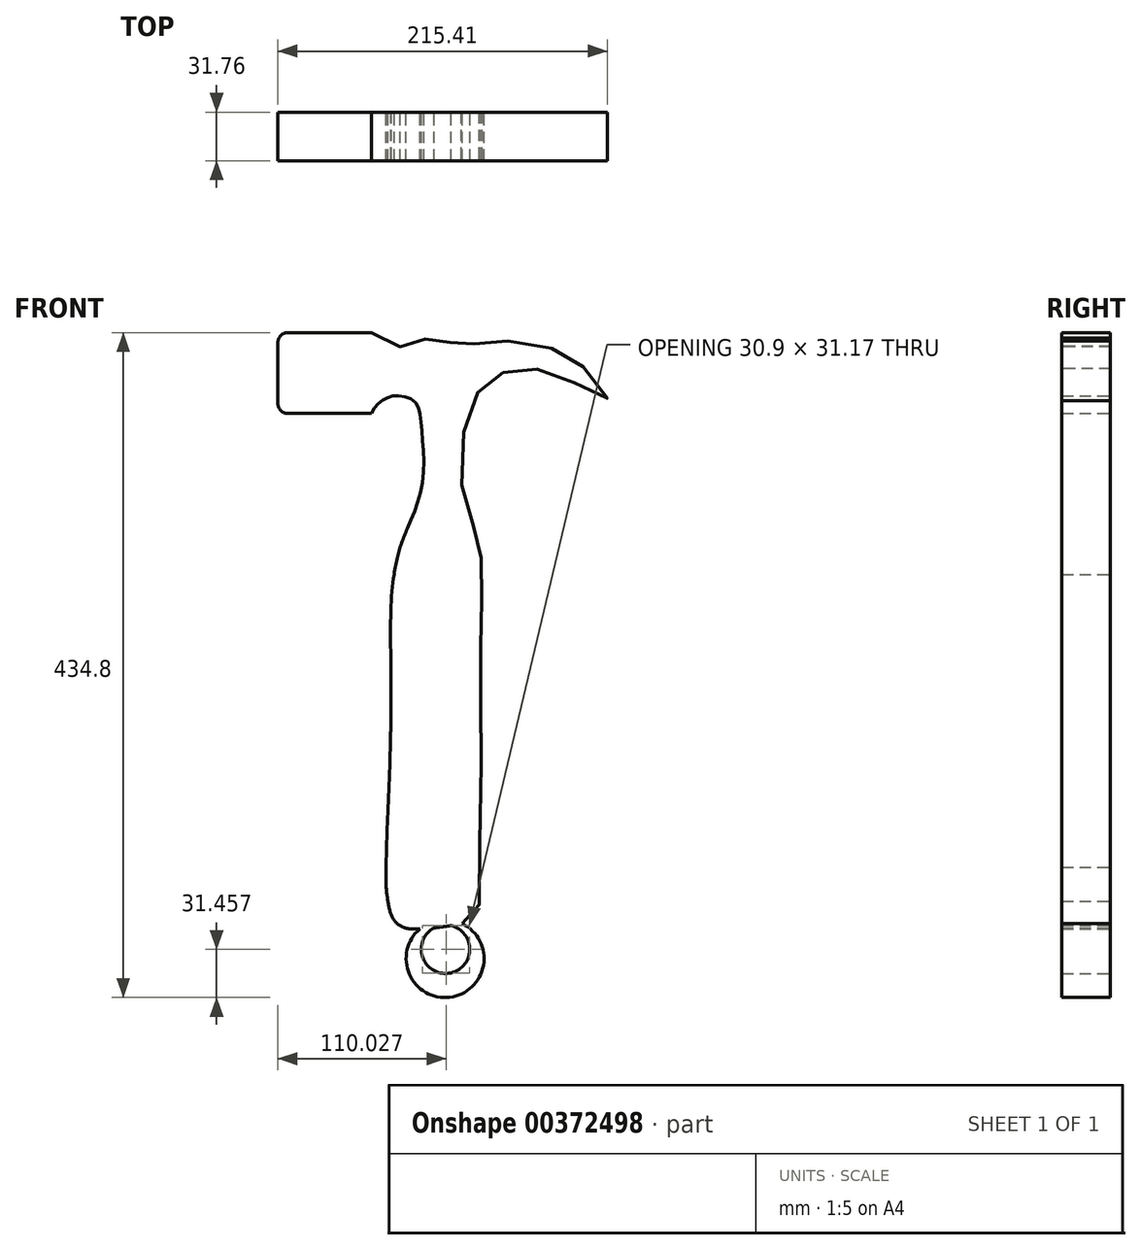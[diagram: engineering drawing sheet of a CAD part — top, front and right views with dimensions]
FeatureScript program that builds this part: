
annotation { "Feature Type Name" : "Feature", "Feature Type Description" : "" }
export const myFeature = defineFeature(function(context is Context, id is Id, definition is map)
    precondition{}
    {
        {
            var Q0;
            Q0=qCreatedBy(makeId("Front.planeOp"),FACE);
            var sketch = newSketch(context, id + "F0", { "sketchPlane" : qUnion([Q0])});
            skPoint(sketch, "E0.middle", {"position": v(-105.81, 53.38) * mm});
            skFitSpline(sketch, "E1", {"points": [v(-78.83, 79.67) * mm, v(-66.18, 71.67) * mm, v(-52.27, 71.24) * mm, v(-44.69, 75.04) * mm, v(-35.41, 75.88) * mm, v(-27.4, 73.35) * mm, v(-24.03, 70.82) * mm, v(-10.96, 72.5) * mm, v(3.8, 74.2) * mm, v(31.62, 71.67) * mm, v(50.41, 63.48) * mm, v(67.03, 50.17) * mm, v(75.04, 35.41) * mm, v(51.07, 48.57) * mm, v(31.07, 55.78) * mm, v(13.7, 55.12) * mm, v(0, 50.04) * mm, v(-11.21, 37.75) * mm, v(-18.97, 11.8) * mm, v(-18.55, -27.82) * mm, v(-11.38, -48.48) * mm, v(-7.59, -62.4) * mm, v(-6.74, -86.42) * mm, v(-7.17, -114.24) * mm, v(-7.38, -154.29) * mm, v(-7.07, -211.58) * mm, v(-8.5, -288.15) * mm, v(-9.89, -303.08) * mm, v(-26.93, -308.09) * mm, v(-60.02, -308.09) * mm, v(-68.04, -292.05) * mm, v(-69.04, -257.96) * mm, v(-66.04, -162.7) * mm, v(-64.03, -78.48) * mm, v(-55.47, -48.44) * mm, v(-51, 9.75) * mm, v(-51, 25.8) * mm, v(-71.78, 25.32) * mm, v(-77.02, 25.32) * mm], "startDerivative": vector(572.27, -465.66) * mm, "endDerivative": vector(-540.88, -56.34) * mm});
            skArc(sketch, "E2", {"start": v(-47.18, -310.27) * mm, "mid": v(-27.63, -354.95) * mm, "end": v(-19.34, -306.9) * mm});
            skArc(sketch, "E3", {"start": v(-37.9, -309.6) * mm, "mid": v(-28.24, -339.26) * mm, "end": v(-26.93, -308.09) * mm});
            skPoint(sketch, "E0.right.start.orphan", {"position": v(-132.8, 27.1) * mm});
            skPoint(sketch, "E0.top.end.orphan", {"position": v(-134.6, 81.44) * mm});
            skLineSegment(sketch, "E4.bottom", {"start": v(-78.83, 79.67) * mm, "end": v(-133.69, 79.67) * mm});
            skLineSegment(sketch, "E4.top", {"start": v(-78.83, 26.88) * mm, "end": v(-133.69, 26.88) * mm});
            skLineSegment(sketch, "E4.left", {"start": v(-78.83, 79.67) * mm, "end": v(-78.83, 26.88) * mm});
            skLineSegment(sketch, "E4.right", {"start": v(-140.04, 73.32) * mm, "end": v(-140.04, 33.23) * mm});
            skPoint(sketch, "E4.middle", {"position": v(-109.43, 53.28) * mm});
            skFitSpline(sketch, "E5", {"points": [v(-78.83, 26.88) * mm, v(-71.78, 35.42) * mm, v(-61.68, 38.52) * mm, v(-50.04, 33.86) * mm, v(-46.15, 17.56) * mm, v(-45.38, -18.16) * mm, v(-55.47, -48.44) * mm, v(-64.03, -78.48) * mm, v(-66.04, -162.7) * mm, v(-69.04, -263.51) * mm, v(-68.04, -292.05) * mm, v(-60.02, -308.09) * mm, v(-47.18, -310.27) * mm], "startDerivative": vector(104.1, 233.41) * mm, "endDerivative": vector(247.77, 9) * mm});
            skPoint(sketch, "E6.visualSharp", {"position": v(-140.04, 79.67) * mm});
            skArc(sketch, "E6.filletArc", {"start": v(-133.69, 79.67) * mm, "mid": v(-138.18, 77.81) * mm, "end": v(-140.04, 73.32) * mm});
            skPoint(sketch, "E7.visualSharp", {"position": v(-140.04, 26.88) * mm});
            skArc(sketch, "E7.filletArc", {"start": v(-140.04, 33.23) * mm, "mid": v(-138.18, 28.74) * mm, "end": v(-133.69, 26.88) * mm});
            skSolve(sketch);
        }
        {
            var Q0;
            Q0 = qSketchRegion(id + "F0", true);
            extrude(context, id + "F1", {"entities" : qUnion([Q0]), "endBound" : BoundingType.SYMMETRIC, "depth" : 31.75 * mm});
        }
    });
